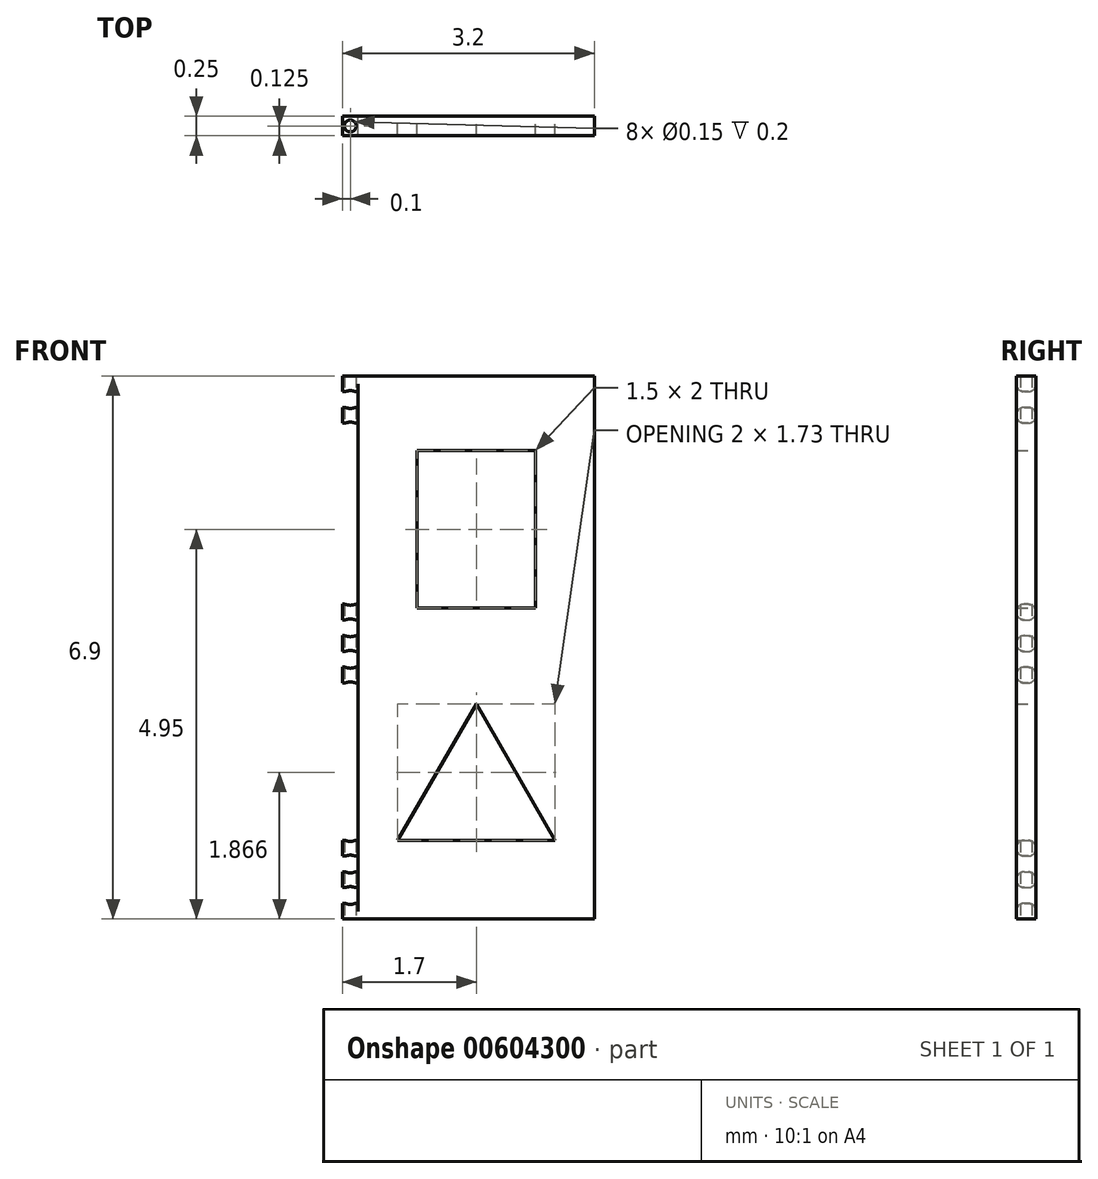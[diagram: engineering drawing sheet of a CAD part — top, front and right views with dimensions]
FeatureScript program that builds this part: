
annotation { "Feature Type Name" : "Feature", "Feature Type Description" : "" }
export const myFeature = defineFeature(function(context is Context, id is Id, definition is map)
    precondition{}
    {
        {
            var Q0;
            Q0=qCreatedBy(makeId("Front.planeOp"),FACE);
            var sketch = newSketch(context, id + "F0", { "sketchPlane" : qUnion([Q0])});
            skLineSegment(sketch, "E0.bottom", {"start": v(1.5, -3.45) * mm, "end": v(-1.5, -3.45) * mm});
            skLineSegment(sketch, "E0.top", {"start": v(1.5, 3.45) * mm, "end": v(-1.5, 3.45) * mm});
            skLineSegment(sketch, "E0.left", {"start": v(1.5, -3.45) * mm, "end": v(1.5, 3.45) * mm});
            skLineSegment(sketch, "E0.right", {"start": v(-1.5, -3.45) * mm, "end": v(-1.5, 3.45) * mm});
            skPoint(sketch, "E0.middle", {"position": v(0, 0) * mm});
            skLineSegment(sketch, "E1.bottom", {"start": v(-0.75, 2.5) * mm, "end": v(0.75, 2.5) * mm});
            skLineSegment(sketch, "E1.top", {"start": v(-0.75, 0.5) * mm, "end": v(0.75, 0.5) * mm});
            skLineSegment(sketch, "E1.left", {"start": v(-0.75, 2.5) * mm, "end": v(-0.75, 0.5) * mm});
            skLineSegment(sketch, "E1.right", {"start": v(0.75, 2.5) * mm, "end": v(0.75, 0.5) * mm});
            skLineSegment(sketch, "E2", {"start": v(0, 0) * mm, "end": v(0, 0.5) * mm});
            skLineSegment(sketch, "E3", {"start": v(0, 0) * mm, "end": v(-1.3, 0) * mm});
            skLineSegment(sketch, "E4", {"start": v(-1, -2.45) * mm, "end": v(1, -2.45) * mm});
            skLineSegment(sketch, "E5", {"start": v(1, -2.45) * mm, "end": v(0, -0.72) * mm});
            skLineSegment(sketch, "E6", {"start": v(0, -0.72) * mm, "end": v(-1, -2.45) * mm});
            skLineSegment(sketch, "E7.bottom", {"start": v(-1.5, 3.45) * mm, "end": v(-1.7, 3.45) * mm});
            skLineSegment(sketch, "E7.top", {"start": v(-1.5, 2.65) * mm, "end": v(-1.7, 2.65) * mm});
            skLineSegment(sketch, "E7.left", {"start": v(-1.5, 3.45) * mm, "end": v(-1.5, 2.65) * mm});
            skLineSegment(sketch, "E7.right", {"start": v(-1.7, 3.45) * mm, "end": v(-1.7, 2.65) * mm});
            skLineSegment(sketch, "E8", {"start": v(-1.5, 3.05) * mm, "end": v(-1.7, 3.05) * mm});
            skLineSegment(sketch, "E9", {"start": v(-1.7, 3.25) * mm, "end": v(-1.5, 3.25) * mm});
            skLineSegment(sketch, "E10", {"start": v(-1.7, 2.85) * mm, "end": v(-1.5, 2.85) * mm});
            skLineSegment(sketch, "E11.bottom", {"start": v(-1.7, 2.65) * mm, "end": v(-1.5, 2.65) * mm});
            skLineSegment(sketch, "E11.top", {"start": v(-1.7, 2.45) * mm, "end": v(-1.5, 2.45) * mm});
            skLineSegment(sketch, "E11.left", {"start": v(-1.7, 2.65) * mm, "end": v(-1.7, 2.45) * mm});
            skLineSegment(sketch, "E11.right", {"start": v(-1.5, 2.65) * mm, "end": v(-1.5, 2.45) * mm});
            skLineSegment(sketch, "E12.MirrorCS", {"start": v(-1.5, -3.45) * mm, "end": v(-1.7, -3.45) * mm});
            skLineSegment(sketch, "E13.MirrorCS", {"start": v(-1.7, -3.45) * mm, "end": v(-1.7, -2.65) * mm});
            skLineSegment(sketch, "E14.MirrorCS", {"start": v(-1.7, -3.25) * mm, "end": v(-1.5, -3.25) * mm});
            skLineSegment(sketch, "E15.MirrorCS", {"start": v(-1.5, -3.05) * mm, "end": v(-1.7, -3.05) * mm});
            skLineSegment(sketch, "E16.MirrorCS", {"start": v(-1.7, -2.85) * mm, "end": v(-1.5, -2.85) * mm});
            skLineSegment(sketch, "E17.MirrorCS", {"start": v(-1.7, -2.65) * mm, "end": v(-1.5, -2.65) * mm});
            skLineSegment(sketch, "E18.MirrorCS", {"start": v(-1.7, -2.65) * mm, "end": v(-1.7, -2.45) * mm});
            skLineSegment(sketch, "E19.MirrorCS", {"start": v(-1.7, -2.45) * mm, "end": v(-1.5, -2.45) * mm});
            skLineSegment(sketch, "E20", {"start": v(-1.3, 0) * mm, "end": v(-1.3, 3) * mm});
            skLineSegment(sketch, "E21", {"start": v(-1.3, 1.5) * mm, "end": v(-1.2, 1.5) * mm});
            skPoint(sketch, "E21.endSnap0", {"position": v(-1.3, 1.5) * mm});
            skLineSegment(sketch, "E22.MirrorCS", {"start": v(-1.7, 0.55) * mm, "end": v(-1.5, 0.55) * mm});
            skLineSegment(sketch, "E23.MirrorCS", {"start": v(-1.7, 0.35) * mm, "end": v(-1.7, 0.55) * mm});
            skLineSegment(sketch, "E24.MirrorCS", {"start": v(-1.7, 0.35) * mm, "end": v(-1.5, 0.35) * mm});
            skLineSegment(sketch, "E25.MirrorCS", {"start": v(-1.7, -0.45) * mm, "end": v(-1.7, 0.35) * mm});
            skLineSegment(sketch, "E26.MirrorCS", {"start": v(-1.7, 0.15) * mm, "end": v(-1.5, 0.15) * mm});
            skLineSegment(sketch, "E27.MirrorCS", {"start": v(-1.5, -0.05) * mm, "end": v(-1.7, -0.05) * mm});
            skLineSegment(sketch, "E28.MirrorCS", {"start": v(-1.7, -0.25) * mm, "end": v(-1.5, -0.25) * mm});
            skLineSegment(sketch, "E29.MirrorCS", {"start": v(-1.5, -0.45) * mm, "end": v(-1.7, -0.45) * mm});
            skSolve(sketch);
        }
        {
            var Q0;
            {var subQ11=sQuery(id+"F0.wireOp",EDGE,"E0.bottom");Q0=makeQuery(id+"F0.imprint","IMPRINT",FACE,{"disambiguationData":[TD([[makeQuery(id+"F0.imprint","IMPRINT",EDGE,{"derivedFrom":subQ11}),-1.0]])]});}
            var Q1;
            {var subQ0=sQuery(id+"F0.wireOp",EDGE,"E12.MirrorCS");Q1=makeQuery(id+"F0.imprint","IMPRINT",FACE,{"disambiguationData":[TD([[makeQuery(id+"F0.imprint","IMPRINT",EDGE,{"derivedFrom":subQ0}),-1.0]])]});}
            var Q2;
            {var subQ0=sQuery(id+"F0.wireOp",EDGE,"E15.MirrorCS");Q2=makeQuery(id+"F0.imprint","IMPRINT",FACE,{"disambiguationData":[TD([[makeQuery(id+"F0.imprint","IMPRINT",EDGE,{"derivedFrom":subQ0}),-1.0]])]});}
            var Q3;
            {var subQ0=sQuery(id+"F0.wireOp",EDGE,"E17.MirrorCS");Q3=makeQuery(id+"F0.imprint","IMPRINT",FACE,{"disambiguationData":[TD([[makeQuery(id+"F0.imprint","IMPRINT",EDGE,{"derivedFrom":subQ0}),1.0]])]});}
            var Q4;
            {var subQ0=sQuery(id+"F0.wireOp",EDGE,"E28.MirrorCS");Q4=makeQuery(id+"F0.imprint","IMPRINT",FACE,{"disambiguationData":[TD([[makeQuery(id+"F0.imprint","IMPRINT",EDGE,{"derivedFrom":subQ0}),-1.0]])]});}
            var Q5;
            {var subQ0=sQuery(id+"F0.wireOp",EDGE,"E26.MirrorCS");Q5=makeQuery(id+"F0.imprint","IMPRINT",FACE,{"disambiguationData":[TD([[makeQuery(id+"F0.imprint","IMPRINT",EDGE,{"derivedFrom":subQ0}),-1.0]])]});}
            var Q6;
            {var subQ0=sQuery(id+"F0.wireOp",EDGE,"E22.MirrorCS");Q6=makeQuery(id+"F0.imprint","IMPRINT",FACE,{"disambiguationData":[TD([[makeQuery(id+"F0.imprint","IMPRINT",EDGE,{"derivedFrom":subQ0}),-1.0]])]});}
            var Q7;
            Q7=makeQuery(id+"F0.imprint","IMPRINT",FACE,{"disambiguationData":[TD([[makeQuery(id+"F0.imprint","IMPRINT",EDGE,{"derivedFrom":sQuery(id+"F0.wireOp",EDGE,"E11.bottom")}),-1.0]])]});
            var Q8;
            {var subQ0=sQuery(id+"F0.wireOp",EDGE,"E8");Q8=makeQuery(id+"F0.imprint","IMPRINT",FACE,{"disambiguationData":[TD([[makeQuery(id+"F0.imprint","IMPRINT",EDGE,{"derivedFrom":subQ0}),1.0]])]});}
            var Q9;
            {var subQ0=sQuery(id+"F0.wireOp",EDGE,"E7.bottom");Q9=makeQuery(id+"F0.imprint","IMPRINT",FACE,{"disambiguationData":[TD([[makeQuery(id+"F0.imprint","IMPRINT",EDGE,{"derivedFrom":subQ0}),1.0]])]});}
            extrude(context, id + "F1", {"entities" : qUnion([Q0, Q1, Q2, Q3, Q4, Q5, Q6, Q7, Q8, Q9]), "depth" : 0.25 * mm, "offsetDistance" : 25 * mm});
        }
        {
            var Q0;
            Q0=makeQuery(id+"F1.opExtrude","SWEPT_FACE",FACE,{"disambiguationData":[OSD([sQuery(id+"F0.wireOp",EDGE,"E0.bottom"),sQuery(id+"F0.wireOp",EDGE,"E12.MirrorCS")])]});
            var sketch = newSketch(context, id + "F2", { "sketchPlane" : qUnion([Q0])});
            skLineSegment(sketch, "E30", {"start": v(-1.7, 0.12) * mm, "end": v(-1.6, 0.12) * mm});
            skCircle(sketch, "E31", {"center": v(-1.6, 0.12) * mm, "radius": 0.07 * mm});
            skSolve(sketch);
        }
        {
            var Q0;
            Q0 = qSketchRegion(id + "F2", true);
            extrude(context, id + "F3", {"entities" : qUnion([Q0]), "operationType" : NewBodyOperationType.REMOVE, "oppositeDirection" : true, "depth" : 25 * mm, "offsetDistance" : 25 * mm});
        }
        {
            var Q0;
            Q0=makeQuery(id+"F1.opExtrude","CAP_EDGE",EDGE,{"disambiguationData":[OSD([sQuery(id+"F0.wireOp",EDGE,"E19.MirrorCS")])],"isStart":false});
            var Q1;
            Q1=makeQuery(id+"F1.opExtrude","CAP_EDGE",EDGE,{"disambiguationData":[OSD([sQuery(id+"F0.wireOp",EDGE,"E19.MirrorCS")])],"isStart":true});
            var Q2;
            Q2=makeQuery(id+"F1.opExtrude","CAP_EDGE",EDGE,{"disambiguationData":[OSD([sQuery(id+"F0.wireOp",EDGE,"E17.MirrorCS")])],"isStart":false});
            var Q3;
            Q3=makeQuery(id+"F1.opExtrude","CAP_EDGE",EDGE,{"disambiguationData":[OSD([sQuery(id+"F0.wireOp",EDGE,"E17.MirrorCS")])],"isStart":true});
            var Q4;
            Q4=makeQuery(id+"F1.opExtrude","CAP_EDGE",EDGE,{"disambiguationData":[OSD([sQuery(id+"F0.wireOp",EDGE,"E16.MirrorCS")])],"isStart":false});
            var Q5;
            Q5=makeQuery(id+"F1.opExtrude","CAP_EDGE",EDGE,{"disambiguationData":[OSD([sQuery(id+"F0.wireOp",EDGE,"E15.MirrorCS")])],"isStart":false});
            var Q6;
            Q6=makeQuery(id+"F1.opExtrude","CAP_EDGE",EDGE,{"disambiguationData":[OSD([sQuery(id+"F0.wireOp",EDGE,"E15.MirrorCS")])],"isStart":true});
            var Q7;
            Q7=makeQuery(id+"F1.opExtrude","CAP_EDGE",EDGE,{"disambiguationData":[OSD([sQuery(id+"F0.wireOp",EDGE,"E16.MirrorCS")])],"isStart":true});
            var Q8;
            Q8=makeQuery(id+"F1.opExtrude","CAP_EDGE",EDGE,{"disambiguationData":[OSD([sQuery(id+"F0.wireOp",EDGE,"E14.MirrorCS")])],"isStart":true});
            var Q9;
            Q9=makeQuery(id+"F1.opExtrude","CAP_EDGE",EDGE,{"disambiguationData":[OSD([sQuery(id+"F0.wireOp",EDGE,"E14.MirrorCS")])],"isStart":false});
            var Q10;
            Q10=makeQuery(id+"F1.opExtrude","CAP_EDGE",EDGE,{"disambiguationData":[OSD([sQuery(id+"F0.wireOp",EDGE,"E28.MirrorCS")])],"isStart":true});
            var Q11;
            Q11=makeQuery(id+"F1.opExtrude","CAP_EDGE",EDGE,{"disambiguationData":[OSD([sQuery(id+"F0.wireOp",EDGE,"E29.MirrorCS")])],"isStart":true});
            var Q12;
            Q12=makeQuery(id+"F1.opExtrude","CAP_EDGE",EDGE,{"disambiguationData":[OSD([sQuery(id+"F0.wireOp",EDGE,"E28.MirrorCS")])],"isStart":false});
            var Q13;
            Q13=makeQuery(id+"F1.opExtrude","CAP_EDGE",EDGE,{"disambiguationData":[OSD([sQuery(id+"F0.wireOp",EDGE,"E29.MirrorCS")])],"isStart":false});
            var Q14;
            Q14=makeQuery(id+"F1.opExtrude","CAP_EDGE",EDGE,{"disambiguationData":[OSD([sQuery(id+"F0.wireOp",EDGE,"E26.MirrorCS")])],"isStart":false});
            var Q15;
            Q15=makeQuery(id+"F1.opExtrude","CAP_EDGE",EDGE,{"disambiguationData":[OSD([sQuery(id+"F0.wireOp",EDGE,"E27.MirrorCS")])],"isStart":false});
            var Q16;
            Q16=makeQuery(id+"F1.opExtrude","CAP_EDGE",EDGE,{"disambiguationData":[OSD([sQuery(id+"F0.wireOp",EDGE,"E26.MirrorCS")])],"isStart":true});
            var Q17;
            Q17=makeQuery(id+"F1.opExtrude","CAP_EDGE",EDGE,{"disambiguationData":[OSD([sQuery(id+"F0.wireOp",EDGE,"E27.MirrorCS")])],"isStart":true});
            var Q18;
            Q18=makeQuery(id+"F1.opExtrude","CAP_EDGE",EDGE,{"disambiguationData":[OSD([sQuery(id+"F0.wireOp",EDGE,"E24.MirrorCS")])],"isStart":true});
            var Q19;
            Q19=makeQuery(id+"F1.opExtrude","CAP_EDGE",EDGE,{"disambiguationData":[OSD([sQuery(id+"F0.wireOp",EDGE,"E22.MirrorCS")])],"isStart":true});
            var Q20;
            Q20=makeQuery(id+"F1.opExtrude","CAP_EDGE",EDGE,{"disambiguationData":[OSD([sQuery(id+"F0.wireOp",EDGE,"E24.MirrorCS")])],"isStart":false});
            var Q21;
            Q21=makeQuery(id+"F1.opExtrude","CAP_EDGE",EDGE,{"disambiguationData":[OSD([sQuery(id+"F0.wireOp",EDGE,"E22.MirrorCS")])],"isStart":false});
            var Q22;
            Q22=makeQuery(id+"F1.opExtrude","CAP_EDGE",EDGE,{"disambiguationData":[OSD([sQuery(id+"F0.wireOp",EDGE,"E11.bottom")])],"isStart":false});
            var Q23;
            Q23=makeQuery(id+"F1.opExtrude","CAP_EDGE",EDGE,{"disambiguationData":[OSD([sQuery(id+"F0.wireOp",EDGE,"E11.bottom")])],"isStart":true});
            var Q24;
            Q24=makeQuery(id+"F1.opExtrude","CAP_EDGE",EDGE,{"disambiguationData":[OSD([sQuery(id+"F0.wireOp",EDGE,"E8")])],"isStart":false});
            var Q25;
            Q25=makeQuery(id+"F1.opExtrude","CAP_EDGE",EDGE,{"disambiguationData":[OSD([sQuery(id+"F0.wireOp",EDGE,"E8")])],"isStart":true});
            var Q26;
            Q26=makeQuery(id+"F1.opExtrude","CAP_EDGE",EDGE,{"disambiguationData":[OSD([sQuery(id+"F0.wireOp",EDGE,"E10")])],"isStart":false});
            var Q27;
            Q27=makeQuery(id+"F1.opExtrude","CAP_EDGE",EDGE,{"disambiguationData":[OSD([sQuery(id+"F0.wireOp",EDGE,"E11.top")])],"isStart":false});
            var Q28;
            Q28=makeQuery(id+"F1.opExtrude","CAP_EDGE",EDGE,{"disambiguationData":[OSD([sQuery(id+"F0.wireOp",EDGE,"E9")])],"isStart":false});
            var Q29;
            Q29=makeQuery(id+"F1.opExtrude","CAP_EDGE",EDGE,{"disambiguationData":[OSD([sQuery(id+"F0.wireOp",EDGE,"E9")])],"isStart":true});
            var Q30;
            Q30=makeQuery(id+"F1.opExtrude","CAP_EDGE",EDGE,{"disambiguationData":[OSD([sQuery(id+"F0.wireOp",EDGE,"E10")])],"isStart":true});
            var Q31;
            Q31=makeQuery(id+"F1.opExtrude","CAP_EDGE",EDGE,{"disambiguationData":[OSD([sQuery(id+"F0.wireOp",EDGE,"E11.top")])],"isStart":true});
            fillet(context, id + "F4", {"entities" : qUnion([Q0, Q1, Q2, Q3, Q4, Q5, Q6, Q7, Q8, Q9, Q10, Q11, Q12, Q13, Q14, Q15, Q16, Q17, Q18, Q19, Q20, Q21, Q22, Q23, Q24, Q25, Q26, Q27, Q28, Q29, Q30, Q31]), "radius" : 0.1 * mm, "tangentPropagation" : true, "allowEdgeOverflow" : false});
        }
    });
